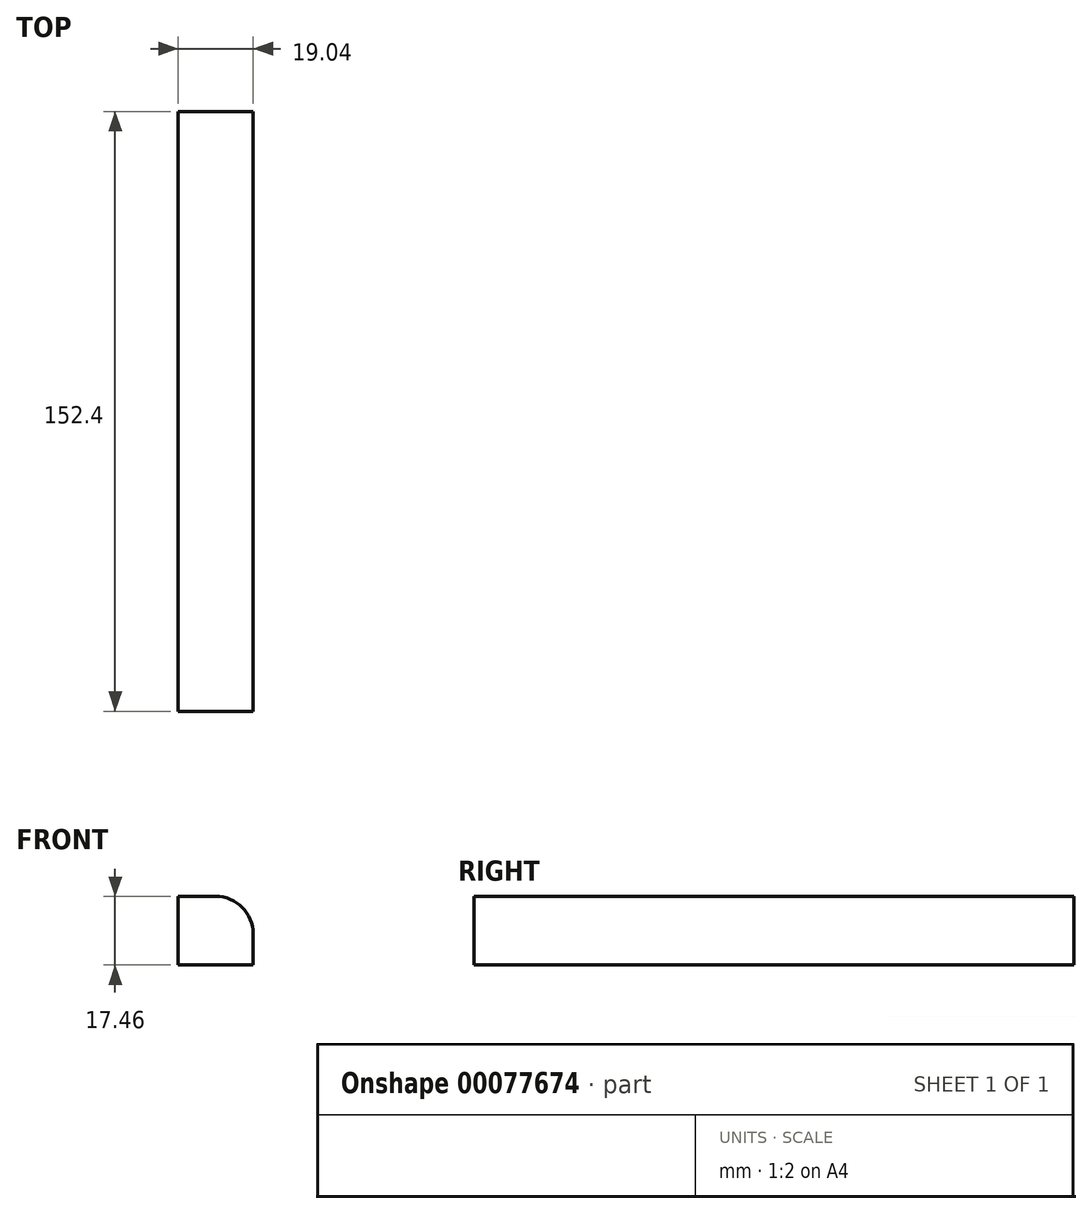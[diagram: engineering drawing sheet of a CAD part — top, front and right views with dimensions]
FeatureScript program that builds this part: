
annotation { "Feature Type Name" : "Feature", "Feature Type Description" : "" }
export const myFeature = defineFeature(function(context is Context, id is Id, definition is map)
    precondition{}
    {
        {
            var Q0;
            Q0=qCreatedBy(makeId("Front.planeOp"),FACE);
            var sketch = newSketch(context, id + "F0", { "sketchPlane" : qUnion([Q0])});
            skLineSegment(sketch, "E0", {"start": v(9.52, -0.8) * mm, "end": v(9.52, -8.73) * mm});
            skLineSegment(sketch, "E1", {"start": v(-9.52, 8.73) * mm, "end": v(0, 8.73) * mm});
            skLineSegment(sketch, "E2", {"start": v(-9.52, 8.73) * mm, "end": v(-9.52, -8.73) * mm});
            skLineSegment(sketch, "E3", {"start": v(-9.52, -8.73) * mm, "end": v(9.52, -8.73) * mm});
            skArc(sketch, "E4", {"start": v(9.52, -0.8) * mm, "mid": v(6.74, 5.94) * mm, "end": v(0, 8.73) * mm});
            skSolve(sketch);
        }
        {
            var Q0;
            Q0=makeQuery(id+"F0.imprint","IMPRINT",FACE,{"disambiguationData":[TD([[makeQuery(id+"F0.imprint","IMPRINT",EDGE,{"derivedFrom":sQuery(id+"F0.wireOp",EDGE,"E0")}),-1.0]])]});
            extrude(context, id + "F1", {"entities" : qUnion([Q0]), "depth" : 152.4 * mm});
        }
    });
